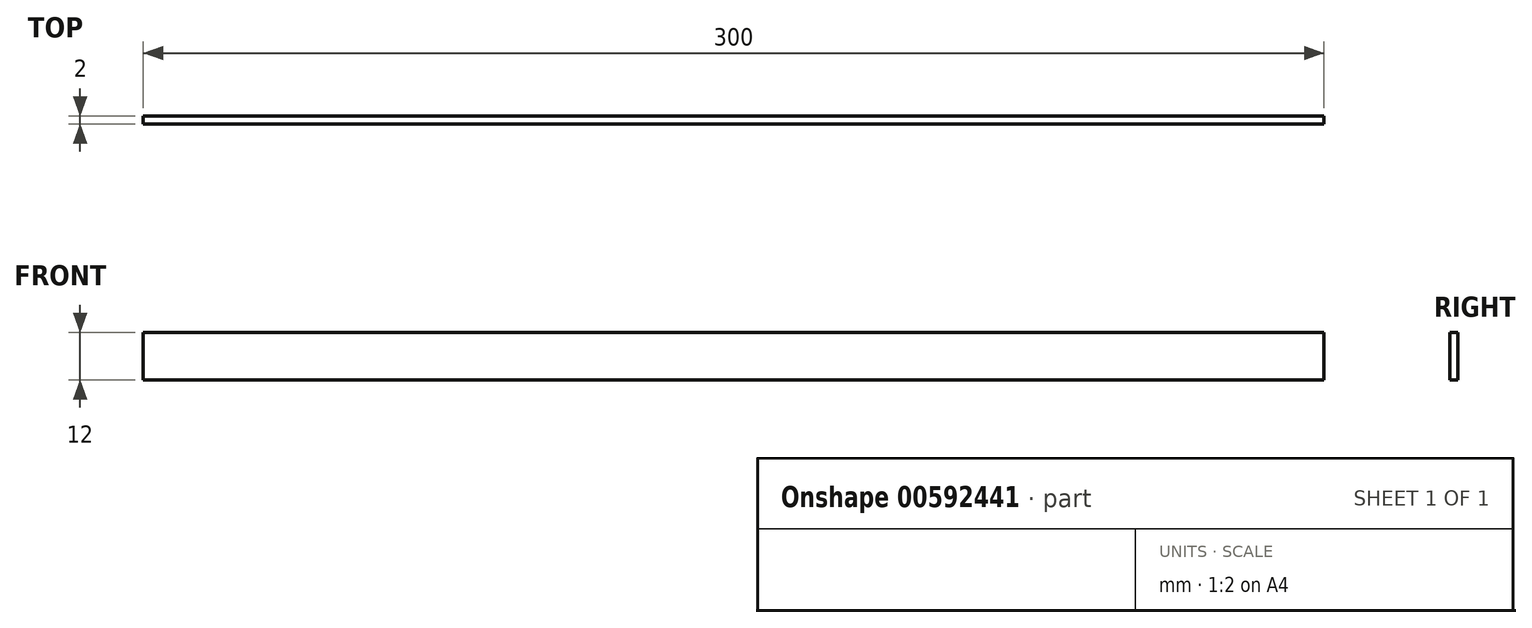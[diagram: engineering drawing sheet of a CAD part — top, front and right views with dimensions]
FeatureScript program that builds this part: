
annotation { "Feature Type Name" : "Feature", "Feature Type Description" : "" }
export const myFeature = defineFeature(function(context is Context, id is Id, definition is map)
    precondition{}
    {
        {
            var Q0;
            Q0=qCreatedBy(makeId("Right.planeOp"),FACE);
            var sketch = newSketch(context, id + "F0", { "sketchPlane" : qUnion([Q0])});
            skLineSegment(sketch, "E0.bottom", {"start": v(1, -6) * mm, "end": v(-1, -6) * mm});
            skLineSegment(sketch, "E0.top", {"start": v(1, 6) * mm, "end": v(-1, 6) * mm});
            skLineSegment(sketch, "E0.left", {"start": v(1, -6) * mm, "end": v(1, 6) * mm});
            skLineSegment(sketch, "E0.right", {"start": v(-1, -6) * mm, "end": v(-1, 6) * mm});
            skPoint(sketch, "E0.middle", {"position": v(0, 0) * mm});
            skSolve(sketch);
        }
        {
            var Q0;
            Q0=makeQuery(id+"F0.imprint","IMPRINT",FACE,{"disambiguationData":[TD([[makeQuery(id+"F0.imprint","IMPRINT",EDGE,{"derivedFrom":sQuery(id+"F0.wireOp",EDGE,"E0.bottom")}),-1.0]])]});
            extrude(context, id + "F1", {"entities" : qUnion([Q0]), "endBound" : BoundingType.SYMMETRIC, "depth" : 300 * mm, "offsetDistance" : 25 * mm});
        }
        {
            var Q0;
            Q0=qCreatedBy(makeId("Right.planeOp"),FACE);
            var sketch = newSketch(context, id + "F2", { "sketchPlane" : qUnion([Q0])});
            skLineSegment(sketch, "E1", {"start": v(-1.16, -3) * mm, "end": v(-1.16, 4.9) * mm});
            skLineSegment(sketch, "E2", {"start": v(1.16, 4.9) * mm, "end": v(1.16, -3) * mm});
            skArc(sketch, "E3", {"start": v(1.28, 5.56) * mm, "mid": v(0, 7.35) * mm, "end": v(-1.28, 5.56) * mm});
            skPoint(sketch, "E4.visualSharp", {"position": v(-1.16, 5.31) * mm});
            skArc(sketch, "E4.filletArc", {"start": v(-1.16, 4.9) * mm, "mid": v(-1.2, 5.23) * mm, "end": v(-1.28, 5.56) * mm});
            skPoint(sketch, "E5.visualSharp", {"position": v(1.16, 5.31) * mm});
            skArc(sketch, "E5.filletArc", {"start": v(1.28, 5.56) * mm, "mid": v(1.2, 5.23) * mm, "end": v(1.16, 4.9) * mm});
            skLineSegment(sketch, "E6", {"start": v(-1.16, -3) * mm, "end": v(1.16, -3) * mm});
            skSolve(sketch);
        }
        {
            var Q0;
            Q0=sQuery(id+"F2.wireOp",EDGE,"E3");
            var Q1;
            Q1=sQuery(id+"F2.wireOp",EDGE,"E4.filletArc");
            var Q2;
            Q2=sQuery(id+"F2.wireOp",EDGE,"E5.filletArc");
            var Q3;
            Q3=sQuery(id+"F2.wireOp",EDGE,"E1");
            var Q4;
            Q4=sQuery(id+"F2.wireOp",EDGE,"E2");
            extrude(context, id + "F3", {"bodyType" : ToolBodyType.SURFACE, "surfaceEntities" : qUnion([Q0, Q1, Q2, Q3, Q4]), "endBound" : BoundingType.SYMMETRIC, "depth" : 290 * mm, "offsetDistance" : 25 * mm});
        }
    });
